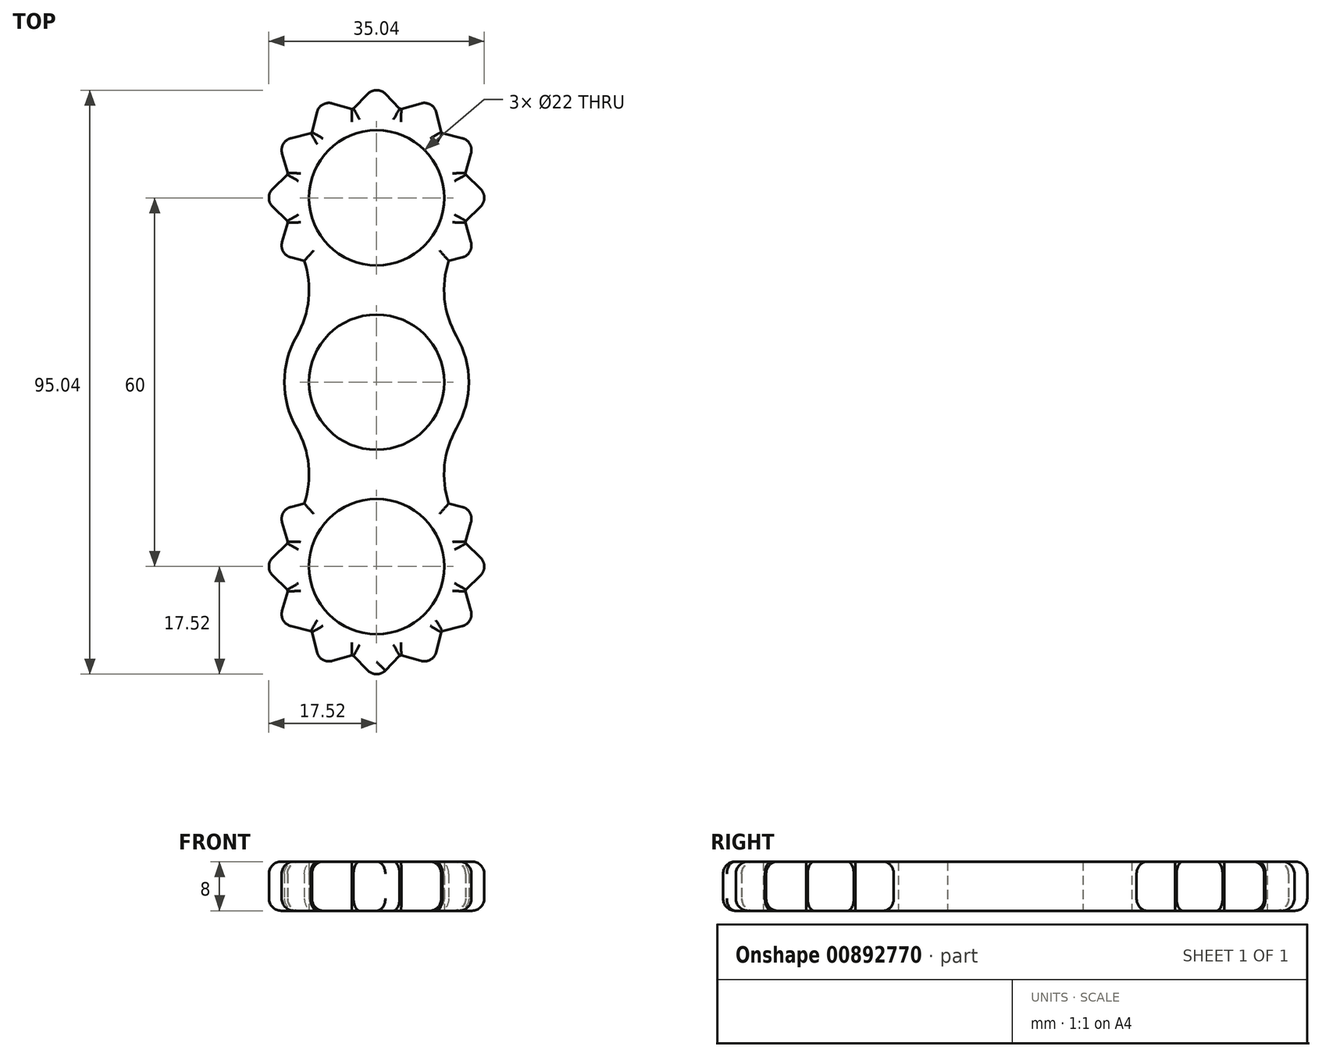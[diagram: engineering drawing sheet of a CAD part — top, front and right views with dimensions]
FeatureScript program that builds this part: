
annotation { "Feature Type Name" : "Feature", "Feature Type Description" : "" }
export const myFeature = defineFeature(function(context is Context, id is Id, definition is map)
    precondition{}
    {
        {
            var Q0;
            Q0=qCreatedBy(makeId("Top.planeOp"),FACE);
            var sketch = newSketch(context, id + "F0", { "sketchPlane" : qUnion([Q0])});
            skArc(sketch, "E0", {"start": v(-13, 7.5) * mm, "mid": v(-15, 0) * mm, "end": v(-13, -7.5) * mm});
            skArc(sketch, "E1", {"start": v(13, 22.5) * mm, "mid": v(0, 45) * mm, "end": v(-13, 22.5) * mm});
            skArc(sketch, "E2", {"start": v(-13, -22.5) * mm, "mid": v(0, -45) * mm, "end": v(13, -22.5) * mm});
            skArc(sketch, "E3", {"start": v(-13, 7.5) * mm, "mid": v(-10.98, 15) * mm, "end": v(-13, 22.5) * mm});
            skArc(sketch, "E4", {"start": v(-13, -22.5) * mm, "mid": v(-10.98, -15) * mm, "end": v(-13, -7.5) * mm});
            skArc(sketch, "E5", {"start": v(13, -7.5) * mm, "mid": v(10.98, -15) * mm, "end": v(13, -22.5) * mm});
            skArc(sketch, "E6", {"start": v(13, 22.5) * mm, "mid": v(10.98, 15) * mm, "end": v(13, 7.5) * mm});
            skArc(sketch, "E7.trimOffspring", {"start": v(13, -7.5) * mm, "mid": v(15, 0) * mm, "end": v(13, 7.5) * mm});
            skLineSegment(sketch, "E8", {"start": v(-15, 0) * mm, "end": v(15, 0) * mm, "construction": true});
            skLineSegment(sketch, "E9", {"start": v(-1.43, 46.91) * mm, "end": v(-3.76, 44.52) * mm});
            skLineSegment(sketch, "E10", {"start": v(1.43, 46.91) * mm, "end": v(3.76, 44.52) * mm});
            skPoint(sketch, "E11.visualSharp", {"position": v(0, 48.39) * mm});
            skArc(sketch, "E11.filletArc", {"start": v(1.43, 46.91) * mm, "mid": v(0, 47.52) * mm, "end": v(-1.43, 46.91) * mm});
            skArc(sketch, "E12.1.0", {"start": v(9.7, 43.93) * mm, "mid": v(8.76, 45.17) * mm, "end": v(7.21, 45.36) * mm});
            skLineSegment(sketch, "E12.1.1", {"start": v(7.21, 45.36) * mm, "end": v(4, 44.45) * mm});
            skLineSegment(sketch, "E12.1.2", {"start": v(9.7, 43.93) * mm, "end": v(10.51, 40.7) * mm});
            skArc(sketch, "E12.2.0", {"start": v(15.36, 37.21) * mm, "mid": v(15.17, 38.76) * mm, "end": v(13.93, 39.7) * mm});
            skLineSegment(sketch, "E12.2.1", {"start": v(13.93, 39.7) * mm, "end": v(10.7, 40.51) * mm});
            skLineSegment(sketch, "E12.2.2", {"start": v(15.36, 37.21) * mm, "end": v(14.45, 34) * mm});
            skArc(sketch, "E12.3.0", {"start": v(16.91, 28.57) * mm, "mid": v(17.52, 30) * mm, "end": v(16.91, 31.43) * mm});
            skLineSegment(sketch, "E12.3.1", {"start": v(16.91, 31.43) * mm, "end": v(14.52, 33.76) * mm});
            skLineSegment(sketch, "E12.3.2", {"start": v(16.91, 28.57) * mm, "end": v(14.52, 26.24) * mm});
            skArc(sketch, "E12.4.0", {"start": v(13.93, 20.3) * mm, "mid": v(15.17, 21.24) * mm, "end": v(15.36, 22.79) * mm});
            skLineSegment(sketch, "E12.4.1", {"start": v(15.36, 22.79) * mm, "end": v(14.45, 26) * mm});
            skLineSegment(sketch, "E12.4.2", {"start": v(13.93, 20.3) * mm, "end": v(11.75, 19.75) * mm});
            skArc(sketch, "E12.8.0", {"start": v(-15.36, 22.79) * mm, "mid": v(-15.17, 21.24) * mm, "end": v(-13.93, 20.3) * mm});
            skLineSegment(sketch, "E12.8.1", {"start": v(-13.93, 20.3) * mm, "end": v(-11.75, 19.75) * mm});
            skLineSegment(sketch, "E12.8.2", {"start": v(-15.36, 22.79) * mm, "end": v(-14.45, 26) * mm});
            skArc(sketch, "E12.9.0", {"start": v(-16.91, 31.43) * mm, "mid": v(-17.52, 30) * mm, "end": v(-16.91, 28.57) * mm});
            skLineSegment(sketch, "E12.9.1", {"start": v(-16.91, 28.57) * mm, "end": v(-14.52, 26.24) * mm});
            skLineSegment(sketch, "E12.9.2", {"start": v(-16.91, 31.43) * mm, "end": v(-14.52, 33.76) * mm});
            skArc(sketch, "E12.10.0", {"start": v(-13.93, 39.7) * mm, "mid": v(-15.17, 38.76) * mm, "end": v(-15.36, 37.21) * mm});
            skLineSegment(sketch, "E12.10.1", {"start": v(-15.36, 37.21) * mm, "end": v(-14.45, 34) * mm});
            skLineSegment(sketch, "E12.10.2", {"start": v(-13.93, 39.7) * mm, "end": v(-10.7, 40.51) * mm});
            skArc(sketch, "E12.11.0", {"start": v(-7.21, 45.36) * mm, "mid": v(-8.76, 45.17) * mm, "end": v(-9.7, 43.93) * mm});
            skLineSegment(sketch, "E12.11.1", {"start": v(-9.7, 43.93) * mm, "end": v(-10.51, 40.7) * mm});
            skLineSegment(sketch, "E12.11.2", {"start": v(-7.21, 45.36) * mm, "end": v(-4, 44.45) * mm});
            skLineSegment(sketch, "E12.anchor1", {"start": v(0, 30) * mm, "end": v(-1.43, 46.91) * mm, "construction": true});
            skLineSegment(sketch, "E12.anchor2", {"start": v(0, 30) * mm, "end": v(-9.7, 43.93) * mm, "construction": true});
            skPoint(sketch, "E13.orphan", {"position": v(-10.7, 19.49) * mm});
            skPoint(sketch, "E14.orphan", {"position": v(10.7, 19.49) * mm});
            skLineSegment(sketch, "E15.MirrorCS", {"start": v(-13.93, -20.3) * mm, "end": v(-11.75, -19.75) * mm});
            skArc(sketch, "E16.MirrorCS", {"start": v(-15.36, -22.79) * mm, "mid": v(-15.17, -21.24) * mm, "end": v(-13.93, -20.3) * mm});
            skLineSegment(sketch, "E17.MirrorCS", {"start": v(-15.36, -22.79) * mm, "end": v(-14.45, -26) * mm});
            skLineSegment(sketch, "E18.MirrorCS", {"start": v(-16.91, -28.57) * mm, "end": v(-14.52, -26.24) * mm});
            skArc(sketch, "E19.MirrorCS", {"start": v(-16.91, -31.43) * mm, "mid": v(-17.52, -30) * mm, "end": v(-16.91, -28.57) * mm});
            skLineSegment(sketch, "E20.MirrorCS", {"start": v(-16.91, -31.43) * mm, "end": v(-14.52, -33.76) * mm});
            skLineSegment(sketch, "E21.MirrorCS", {"start": v(-15.36, -37.21) * mm, "end": v(-14.45, -34) * mm});
            skArc(sketch, "E22.MirrorCS", {"start": v(-13.93, -39.7) * mm, "mid": v(-15.17, -38.76) * mm, "end": v(-15.36, -37.21) * mm});
            skLineSegment(sketch, "E23.MirrorCS", {"start": v(-13.93, -39.7) * mm, "end": v(-10.7, -40.51) * mm});
            skLineSegment(sketch, "E24.MirrorCS", {"start": v(-9.7, -43.93) * mm, "end": v(-10.51, -40.7) * mm});
            skArc(sketch, "E25.MirrorCS", {"start": v(-7.21, -45.36) * mm, "mid": v(-8.76, -45.17) * mm, "end": v(-9.7, -43.93) * mm});
            skLineSegment(sketch, "E26.MirrorCS", {"start": v(-7.21, -45.36) * mm, "end": v(-4, -44.45) * mm});
            skLineSegment(sketch, "E27.MirrorCS", {"start": v(-1.43, -46.91) * mm, "end": v(-3.76, -44.52) * mm});
            skArc(sketch, "E28.MirrorCS", {"start": v(1.43, -46.91) * mm, "mid": v(0, -47.52) * mm, "end": v(-1.43, -46.91) * mm});
            skLineSegment(sketch, "E29.MirrorCS", {"start": v(1.43, -46.91) * mm, "end": v(3.76, -44.52) * mm});
            skLineSegment(sketch, "E30.MirrorCS", {"start": v(7.21, -45.36) * mm, "end": v(4, -44.45) * mm});
            skArc(sketch, "E31.MirrorCS", {"start": v(9.7, -43.93) * mm, "mid": v(8.76, -45.17) * mm, "end": v(7.21, -45.36) * mm});
            skLineSegment(sketch, "E32.MirrorCS", {"start": v(9.7, -43.93) * mm, "end": v(10.51, -40.7) * mm});
            skLineSegment(sketch, "E33.MirrorCS", {"start": v(13.93, -39.7) * mm, "end": v(10.7, -40.51) * mm});
            skArc(sketch, "E34.MirrorCS", {"start": v(15.36, -37.21) * mm, "mid": v(15.17, -38.76) * mm, "end": v(13.93, -39.7) * mm});
            skLineSegment(sketch, "E35.MirrorCS", {"start": v(15.36, -37.21) * mm, "end": v(14.45, -34) * mm});
            skLineSegment(sketch, "E36.MirrorCS", {"start": v(16.91, -31.43) * mm, "end": v(14.52, -33.76) * mm});
            skArc(sketch, "E37.MirrorCS", {"start": v(16.91, -28.57) * mm, "mid": v(17.52, -30) * mm, "end": v(16.91, -31.43) * mm});
            skLineSegment(sketch, "E38.MirrorCS", {"start": v(16.91, -28.57) * mm, "end": v(14.52, -26.24) * mm});
            skLineSegment(sketch, "E39.MirrorCS", {"start": v(15.36, -22.79) * mm, "end": v(14.45, -26) * mm});
            skArc(sketch, "E40.MirrorCS", {"start": v(13.93, -20.3) * mm, "mid": v(15.17, -21.24) * mm, "end": v(15.36, -22.79) * mm});
            skLineSegment(sketch, "E41.MirrorCS", {"start": v(13.93, -20.3) * mm, "end": v(11.75, -19.75) * mm});
            skSolve(sketch);
        }
        {
            var Q0;
            {var subQ0=sQuery(id+"F0.wireOp",EDGE,"E18.MirrorCS");Q0=makeQuery(id+"F0.imprint","IMPRINT",FACE,{"disambiguationData":[TD([[makeQuery(id+"F0.imprint","IMPRINT",EDGE,{"derivedFrom":subQ0}),-1.0]])]});}
            var Q1;
            Q1=makeQuery(id+"F0.imprint","IMPRINT",FACE,{"disambiguationData":[TD([[makeQuery(id+"F0.imprint","IMPRINT",EDGE,{"derivedFrom":sQuery(id+"F0.wireOp",EDGE,"E12.10.0")}),1.0]])]});
            var Q2;
            Q2=makeQuery(id+"F0.imprint","IMPRINT",FACE,{"disambiguationData":[TD([[makeQuery(id+"F0.imprint","IMPRINT",EDGE,{"derivedFrom":sQuery(id+"F0.wireOp",EDGE,"E12.9.0")}),1.0]])]});
            var Q3;
            {var subQ23=sQuery(id+"F0.wireOp",EDGE,"E0");Q3=makeQuery(id+"F0.imprint","IMPRINT",FACE,{"disambiguationData":[TD([[makeQuery(id+"F0.imprint","IMPRINT",EDGE,{"derivedFrom":subQ23}),1.0]])]});}
            var Q4;
            {var subQ0=sQuery(id+"F0.wireOp",EDGE,"E15.MirrorCS");Q4=makeQuery(id+"F0.imprint","IMPRINT",FACE,{"disambiguationData":[TD([[makeQuery(id+"F0.imprint","IMPRINT",EDGE,{"derivedFrom":subQ0}),-1.0]])]});}
            var Q5;
            {var subQ0=sQuery(id+"F0.wireOp",EDGE,"E36.MirrorCS");Q5=makeQuery(id+"F0.imprint","IMPRINT",FACE,{"disambiguationData":[TD([[makeQuery(id+"F0.imprint","IMPRINT",EDGE,{"derivedFrom":subQ0}),-1.0]])]});}
            var Q6;
            Q6=makeQuery(id+"F0.imprint","IMPRINT",FACE,{"disambiguationData":[TD([[makeQuery(id+"F0.imprint","IMPRINT",EDGE,{"derivedFrom":sQuery(id+"F0.wireOp",EDGE,"E12.2.0")}),1.0]])]});
            var Q7;
            {var subQ0=sQuery(id+"F0.wireOp",EDGE,"E9");Q7=makeQuery(id+"F0.imprint","IMPRINT",FACE,{"disambiguationData":[TD([[makeQuery(id+"F0.imprint","IMPRINT",EDGE,{"derivedFrom":subQ0}),1.0]])]});}
            var Q8;
            Q8=makeQuery(id+"F0.imprint","IMPRINT",FACE,{"disambiguationData":[TD([[makeQuery(id+"F0.imprint","IMPRINT",EDGE,{"derivedFrom":sQuery(id+"F0.wireOp",EDGE,"E12.4.0")}),1.0]])]});
            var Q9;
            {var subQ0=sQuery(id+"F0.wireOp",EDGE,"E39.MirrorCS");Q9=makeQuery(id+"F0.imprint","IMPRINT",FACE,{"disambiguationData":[TD([[makeQuery(id+"F0.imprint","IMPRINT",EDGE,{"derivedFrom":subQ0}),-1.0]])]});}
            var Q10;
            {var subQ0=sQuery(id+"F0.wireOp",EDGE,"E30.MirrorCS");Q10=makeQuery(id+"F0.imprint","IMPRINT",FACE,{"disambiguationData":[TD([[makeQuery(id+"F0.imprint","IMPRINT",EDGE,{"derivedFrom":subQ0}),-1.0]])]});}
            var Q11;
            {var subQ0=sQuery(id+"F0.wireOp",EDGE,"E33.MirrorCS");Q11=makeQuery(id+"F0.imprint","IMPRINT",FACE,{"disambiguationData":[TD([[makeQuery(id+"F0.imprint","IMPRINT",EDGE,{"derivedFrom":subQ0}),-1.0]])]});}
            var Q12;
            {var subQ0=sQuery(id+"F0.wireOp",EDGE,"E21.MirrorCS");Q12=makeQuery(id+"F0.imprint","IMPRINT",FACE,{"disambiguationData":[TD([[makeQuery(id+"F0.imprint","IMPRINT",EDGE,{"derivedFrom":subQ0}),-1.0]])]});}
            var Q13;
            Q13=makeQuery(id+"F0.imprint","IMPRINT",FACE,{"disambiguationData":[TD([[makeQuery(id+"F0.imprint","IMPRINT",EDGE,{"derivedFrom":sQuery(id+"F0.wireOp",EDGE,"E12.3.0")}),1.0]])]});
            var Q14;
            Q14=makeQuery(id+"F0.imprint","IMPRINT",FACE,{"disambiguationData":[TD([[makeQuery(id+"F0.imprint","IMPRINT",EDGE,{"derivedFrom":sQuery(id+"F0.wireOp",EDGE,"E12.1.0")}),1.0]])]});
            var Q15;
            {var subQ0=sQuery(id+"F0.wireOp",EDGE,"E24.MirrorCS");Q15=makeQuery(id+"F0.imprint","IMPRINT",FACE,{"disambiguationData":[TD([[makeQuery(id+"F0.imprint","IMPRINT",EDGE,{"derivedFrom":subQ0}),-1.0]])]});}
            var Q16;
            Q16=makeQuery(id+"F0.imprint","IMPRINT",FACE,{"disambiguationData":[TD([[makeQuery(id+"F0.imprint","IMPRINT",EDGE,{"derivedFrom":sQuery(id+"F0.wireOp",EDGE,"E12.11.0")}),1.0]])]});
            var Q17;
            Q17=makeQuery(id+"F0.imprint","IMPRINT",FACE,{"disambiguationData":[TD([[makeQuery(id+"F0.imprint","IMPRINT",EDGE,{"derivedFrom":sQuery(id+"F0.wireOp",EDGE,"E12.8.0")}),1.0]])]});
            var Q18;
            {var subQ0=sQuery(id+"F0.wireOp",EDGE,"E27.MirrorCS");Q18=makeQuery(id+"F0.imprint","IMPRINT",FACE,{"disambiguationData":[TD([[makeQuery(id+"F0.imprint","IMPRINT",EDGE,{"derivedFrom":subQ0}),-1.0]])]});}
            extrude(context, id + "F1", {"entities" : qUnion([Q0, Q1, Q2, Q3, Q4, Q5, Q6, Q7, Q8, Q9, Q10, Q11, Q12, Q13, Q14, Q15, Q16, Q17, Q18]), "depth" : 8 * mm, "offsetDistance" : 25 * mm});
        }
        {
            var Q0;
            Q0=sQuery(id+"F0.wireOp",VERTEX,"E2.center");
            var Q1;
            Q1=sQuery(id+"F0.wireOp",VERTEX,"E0.center");
            var Q2;
            Q2=sQuery(id+"F0.wireOp",VERTEX,"E1.center");
            var Q3;
            Q3=makeQuery(id+"F1.opExtrude","SWEPT_BODY",BODY,{"disambiguationData":[OSD([sQuery(id+"F0.wireOp",EDGE,"E0"),sQuery(id+"F0.wireOp",EDGE,"E1"),sQuery(id+"F0.wireOp",EDGE,"E2"),sQuery(id+"F0.wireOp",EDGE,"E3"),sQuery(id+"F0.wireOp",EDGE,"E4"),sQuery(id+"F0.wireOp",EDGE,"E5"),sQuery(id+"F0.wireOp",EDGE,"E6"),sQuery(id+"F0.wireOp",EDGE,"E7.trimOffspring"),sQuery(id+"F0.wireOp",EDGE,"E9"),sQuery(id+"F0.wireOp",EDGE,"E10"),sQuery(id+"F0.wireOp",EDGE,"E11.filletArc"),sQuery(id+"F0.wireOp",EDGE,"E12.1.0"),sQuery(id+"F0.wireOp",EDGE,"E12.1.1"),sQuery(id+"F0.wireOp",EDGE,"E12.1.2"),sQuery(id+"F0.wireOp",EDGE,"E12.2.0"),sQuery(id+"F0.wireOp",EDGE,"E12.2.1"),sQuery(id+"F0.wireOp",EDGE,"E12.2.2"),sQuery(id+"F0.wireOp",EDGE,"E12.3.0"),sQuery(id+"F0.wireOp",EDGE,"E12.3.1"),sQuery(id+"F0.wireOp",EDGE,"E12.3.2"),sQuery(id+"F0.wireOp",EDGE,"E12.4.0"),sQuery(id+"F0.wireOp",EDGE,"E12.4.1"),sQuery(id+"F0.wireOp",EDGE,"E12.4.2"),sQuery(id+"F0.wireOp",EDGE,"E12.8.0"),sQuery(id+"F0.wireOp",EDGE,"E12.8.1"),sQuery(id+"F0.wireOp",EDGE,"E12.8.2"),sQuery(id+"F0.wireOp",EDGE,"E12.9.0"),sQuery(id+"F0.wireOp",EDGE,"E12.9.1"),sQuery(id+"F0.wireOp",EDGE,"E12.9.2"),sQuery(id+"F0.wireOp",EDGE,"E12.10.0"),sQuery(id+"F0.wireOp",EDGE,"E12.10.1"),sQuery(id+"F0.wireOp",EDGE,"E12.10.2"),sQuery(id+"F0.wireOp",EDGE,"E12.11.0"),sQuery(id+"F0.wireOp",EDGE,"E12.11.1"),sQuery(id+"F0.wireOp",EDGE,"E12.11.2"),sQuery(id+"F0.wireOp",EDGE,"E15.MirrorCS"),sQuery(id+"F0.wireOp",EDGE,"E16.MirrorCS"),sQuery(id+"F0.wireOp",EDGE,"E17.MirrorCS"),sQuery(id+"F0.wireOp",EDGE,"E18.MirrorCS"),sQuery(id+"F0.wireOp",EDGE,"E19.MirrorCS"),sQuery(id+"F0.wireOp",EDGE,"E20.MirrorCS"),sQuery(id+"F0.wireOp",EDGE,"E21.MirrorCS"),sQuery(id+"F0.wireOp",EDGE,"E22.MirrorCS"),sQuery(id+"F0.wireOp",EDGE,"E23.MirrorCS"),sQuery(id+"F0.wireOp",EDGE,"E24.MirrorCS"),sQuery(id+"F0.wireOp",EDGE,"E25.MirrorCS"),sQuery(id+"F0.wireOp",EDGE,"E26.MirrorCS"),sQuery(id+"F0.wireOp",EDGE,"E27.MirrorCS"),sQuery(id+"F0.wireOp",EDGE,"E28.MirrorCS"),sQuery(id+"F0.wireOp",EDGE,"E29.MirrorCS"),sQuery(id+"F0.wireOp",EDGE,"E30.MirrorCS"),sQuery(id+"F0.wireOp",EDGE,"E31.MirrorCS"),sQuery(id+"F0.wireOp",EDGE,"E32.MirrorCS"),sQuery(id+"F0.wireOp",EDGE,"E33.MirrorCS"),sQuery(id+"F0.wireOp",EDGE,"E34.MirrorCS"),sQuery(id+"F0.wireOp",EDGE,"E35.MirrorCS"),sQuery(id+"F0.wireOp",EDGE,"E36.MirrorCS"),sQuery(id+"F0.wireOp",EDGE,"E37.MirrorCS"),sQuery(id+"F0.wireOp",EDGE,"E38.MirrorCS"),sQuery(id+"F0.wireOp",EDGE,"E39.MirrorCS"),sQuery(id+"F0.wireOp",EDGE,"E40.MirrorCS"),sQuery(id+"F0.wireOp",EDGE,"E41.MirrorCS")])]});
            hole(context, id + "F2", {"style" : HoleStyle.SIMPLE, "endStyle" : HoleEndStyle.THROUGH, "oppositeDirection" : true, "holeDiameter" : 22 * mm, "majorDiameter" : 5 * mm, "isTappedThrough" : true, "tappedDepth" : 12 * mm, "tapClearance" : 3, "locations" : qUnion([Q0, Q1, Q2]), "scope" : qUnion([Q3])});
        }
        {
            var Q0;
            Q0=makeQuery(id+"F1.opExtrude","CAP_EDGE",EDGE,{"disambiguationData":[OSD([sQuery(id+"F0.wireOp",EDGE,"E7.trimOffspring")])],"isStart":false});
            var Q1;
            Q1=makeQuery(id+"F1.opExtrude","CAP_EDGE",EDGE,{"disambiguationData":[OSD([sQuery(id+"F0.wireOp",EDGE,"E5")])],"isStart":false});
            var Q2;
            Q2=makeQuery(id+"F1.opExtrude","CAP_EDGE",EDGE,{"disambiguationData":[OSD([sQuery(id+"F0.wireOp",EDGE,"E41.MirrorCS")])],"isStart":false});
            var Q3;
            Q3=makeQuery(id+"F1.opExtrude","CAP_EDGE",EDGE,{"disambiguationData":[OSD([sQuery(id+"F0.wireOp",EDGE,"E39.MirrorCS")])],"isStart":false});
            var Q4;
            {var subQ0=sQuery(id+"F0.wireOp",EDGE,"E2");Q4=makeQuery(id+"F1.opExtrude","CAP_EDGE",EDGE,{"disambiguationData":[OSD([subQ0]),TDD([makeQuery(id+"F0.imprint","IMPRINT",EDGE,{"disambiguationData":[TD([[makeQuery(id+"F0.imprint","INTERSECT",VERTEX,{"derivedFrom":[subQ0,sQuery(id+"F0.wireOp",EDGE,"E38.MirrorCS")]}),-1.0]])],"derivedFrom":subQ0})])],"isStart":false});}
            var Q5;
            Q5=makeQuery(id+"F1.opExtrude","CAP_EDGE",EDGE,{"disambiguationData":[OSD([sQuery(id+"F0.wireOp",EDGE,"E38.MirrorCS")])],"isStart":false});
            var Q6;
            Q6=makeQuery(id+"F1.opExtrude","CAP_EDGE",EDGE,{"disambiguationData":[OSD([sQuery(id+"F0.wireOp",EDGE,"E36.MirrorCS")])],"isStart":false});
            var Q7;
            {var subQ0=sQuery(id+"F0.wireOp",EDGE,"E2");Q7=makeQuery(id+"F1.opExtrude","CAP_EDGE",EDGE,{"disambiguationData":[OSD([subQ0]),TDD([makeQuery(id+"F0.imprint","IMPRINT",EDGE,{"disambiguationData":[TD([[makeQuery(id+"F0.imprint","INTERSECT",VERTEX,{"derivedFrom":[subQ0,sQuery(id+"F0.wireOp",EDGE,"E35.MirrorCS")]}),-1.0]])],"derivedFrom":subQ0})])],"isStart":false});}
            var Q8;
            Q8=makeQuery(id+"F1.opExtrude","CAP_EDGE",EDGE,{"disambiguationData":[OSD([sQuery(id+"F0.wireOp",EDGE,"E35.MirrorCS")])],"isStart":false});
            var Q9;
            Q9=makeQuery(id+"F1.opExtrude","CAP_EDGE",EDGE,{"disambiguationData":[OSD([sQuery(id+"F0.wireOp",EDGE,"E33.MirrorCS")])],"isStart":false});
            var Q10;
            {var subQ0=sQuery(id+"F0.wireOp",EDGE,"E2");Q10=makeQuery(id+"F1.opExtrude","CAP_EDGE",EDGE,{"disambiguationData":[OSD([subQ0]),TDD([makeQuery(id+"F0.imprint","IMPRINT",EDGE,{"disambiguationData":[TD([[makeQuery(id+"F0.imprint","INTERSECT",VERTEX,{"derivedFrom":[subQ0,sQuery(id+"F0.wireOp",EDGE,"E32.MirrorCS")]}),-1.0]])],"derivedFrom":subQ0})])],"isStart":false});}
            var Q11;
            Q11=makeQuery(id+"F1.opExtrude","CAP_EDGE",EDGE,{"disambiguationData":[OSD([sQuery(id+"F0.wireOp",EDGE,"E32.MirrorCS")])],"isStart":false});
            var Q12;
            Q12=makeQuery(id+"F1.opExtrude","CAP_EDGE",EDGE,{"disambiguationData":[OSD([sQuery(id+"F0.wireOp",EDGE,"E30.MirrorCS")])],"isStart":false});
            var Q13;
            {var subQ0=sQuery(id+"F0.wireOp",EDGE,"E2");Q13=makeQuery(id+"F1.opExtrude","CAP_EDGE",EDGE,{"disambiguationData":[OSD([subQ0]),TDD([makeQuery(id+"F0.imprint","IMPRINT",EDGE,{"disambiguationData":[TD([[makeQuery(id+"F0.imprint","INTERSECT",VERTEX,{"derivedFrom":[subQ0,sQuery(id+"F0.wireOp",EDGE,"E29.MirrorCS")]}),-1.0]])],"derivedFrom":subQ0})])],"isStart":false});}
            var Q14;
            Q14=makeQuery(id+"F1.opExtrude","CAP_EDGE",EDGE,{"disambiguationData":[OSD([sQuery(id+"F0.wireOp",EDGE,"E29.MirrorCS")])],"isStart":false});
            var Q15;
            Q15=makeQuery(id+"F1.opExtrude","CAP_EDGE",EDGE,{"disambiguationData":[OSD([sQuery(id+"F0.wireOp",EDGE,"E27.MirrorCS")])],"isStart":false});
            var Q16;
            {var subQ0=sQuery(id+"F0.wireOp",EDGE,"E2");Q16=makeQuery(id+"F1.opExtrude","CAP_EDGE",EDGE,{"disambiguationData":[OSD([subQ0]),TDD([makeQuery(id+"F0.imprint","IMPRINT",EDGE,{"disambiguationData":[TD([[makeQuery(id+"F0.imprint","INTERSECT",VERTEX,{"derivedFrom":[subQ0,sQuery(id+"F0.wireOp",EDGE,"E26.MirrorCS")]}),-1.0]])],"derivedFrom":subQ0})])],"isStart":false});}
            var Q17;
            Q17=makeQuery(id+"F1.opExtrude","CAP_EDGE",EDGE,{"disambiguationData":[OSD([sQuery(id+"F0.wireOp",EDGE,"E26.MirrorCS")])],"isStart":false});
            var Q18;
            {var subQ0=sQuery(id+"F0.wireOp",EDGE,"E2");Q18=makeQuery(id+"F1.opExtrude","CAP_EDGE",EDGE,{"disambiguationData":[OSD([subQ0]),TDD([makeQuery(id+"F0.imprint","IMPRINT",EDGE,{"disambiguationData":[TD([[makeQuery(id+"F0.imprint","INTERSECT",VERTEX,{"derivedFrom":[subQ0,sQuery(id+"F0.wireOp",EDGE,"E23.MirrorCS")]}),-1.0]])],"derivedFrom":subQ0})])],"isStart":false});}
            var Q19;
            Q19=makeQuery(id+"F1.opExtrude","CAP_EDGE",EDGE,{"disambiguationData":[OSD([sQuery(id+"F0.wireOp",EDGE,"E24.MirrorCS")])],"isStart":false});
            var Q20;
            Q20=makeQuery(id+"F1.opExtrude","CAP_EDGE",EDGE,{"disambiguationData":[OSD([sQuery(id+"F0.wireOp",EDGE,"E23.MirrorCS")])],"isStart":false});
            var Q21;
            Q21=makeQuery(id+"F1.opExtrude","CAP_EDGE",EDGE,{"disambiguationData":[OSD([sQuery(id+"F0.wireOp",EDGE,"E21.MirrorCS")])],"isStart":false});
            var Q22;
            {var subQ0=sQuery(id+"F0.wireOp",EDGE,"E2");Q22=makeQuery(id+"F1.opExtrude","CAP_EDGE",EDGE,{"disambiguationData":[OSD([subQ0]),TDD([makeQuery(id+"F0.imprint","IMPRINT",EDGE,{"disambiguationData":[TD([[makeQuery(id+"F0.imprint","INTERSECT",VERTEX,{"derivedFrom":[subQ0,sQuery(id+"F0.wireOp",EDGE,"E20.MirrorCS")]}),-1.0]])],"derivedFrom":subQ0})])],"isStart":false});}
            var Q23;
            Q23=makeQuery(id+"F1.opExtrude","CAP_EDGE",EDGE,{"disambiguationData":[OSD([sQuery(id+"F0.wireOp",EDGE,"E20.MirrorCS")])],"isStart":false});
            var Q24;
            {var subQ0=sQuery(id+"F0.wireOp",EDGE,"E2");Q24=makeQuery(id+"F1.opExtrude","CAP_EDGE",EDGE,{"disambiguationData":[OSD([subQ0]),TDD([makeQuery(id+"F0.imprint","IMPRINT",EDGE,{"disambiguationData":[TD([[makeQuery(id+"F0.imprint","INTERSECT",VERTEX,{"derivedFrom":[subQ0,sQuery(id+"F0.wireOp",EDGE,"E17.MirrorCS")]}),-1.0]])],"derivedFrom":subQ0})])],"isStart":false});}
            var Q25;
            Q25=makeQuery(id+"F1.opExtrude","CAP_EDGE",EDGE,{"disambiguationData":[OSD([sQuery(id+"F0.wireOp",EDGE,"E17.MirrorCS")])],"isStart":false});
            var Q26;
            Q26=makeQuery(id+"F1.opExtrude","CAP_EDGE",EDGE,{"disambiguationData":[OSD([sQuery(id+"F0.wireOp",EDGE,"E15.MirrorCS")])],"isStart":false});
            var Q27;
            Q27=makeQuery(id+"F1.opExtrude","CAP_EDGE",EDGE,{"disambiguationData":[OSD([sQuery(id+"F0.wireOp",EDGE,"E4")])],"isStart":false});
            var Q28;
            Q28=makeQuery(id+"F1.opExtrude","CAP_EDGE",EDGE,{"disambiguationData":[OSD([sQuery(id+"F0.wireOp",EDGE,"E0")])],"isStart":false});
            var Q29;
            Q29=makeQuery(id+"F1.opExtrude","CAP_EDGE",EDGE,{"disambiguationData":[OSD([sQuery(id+"F0.wireOp",EDGE,"E3")])],"isStart":false});
            var Q30;
            Q30=makeQuery(id+"F1.opExtrude","CAP_EDGE",EDGE,{"disambiguationData":[OSD([sQuery(id+"F0.wireOp",EDGE,"E12.8.1")])],"isStart":false});
            var Q31;
            Q31=makeQuery(id+"F1.opExtrude","CAP_EDGE",EDGE,{"disambiguationData":[OSD([sQuery(id+"F0.wireOp",EDGE,"E12.8.2")])],"isStart":false});
            var Q32;
            Q32=makeQuery(id+"F1.opExtrude","CAP_EDGE",EDGE,{"disambiguationData":[OSD([sQuery(id+"F0.wireOp",EDGE,"E12.9.1")])],"isStart":false});
            var Q33;
            Q33=makeQuery(id+"F1.opExtrude","CAP_EDGE",EDGE,{"disambiguationData":[OSD([sQuery(id+"F0.wireOp",EDGE,"E12.9.2")])],"isStart":false});
            var Q34;
            Q34=makeQuery(id+"F1.opExtrude","CAP_EDGE",EDGE,{"disambiguationData":[OSD([sQuery(id+"F0.wireOp",EDGE,"E12.10.2")])],"isStart":false});
            var Q35;
            Q35=makeQuery(id+"F1.opExtrude","CAP_EDGE",EDGE,{"disambiguationData":[OSD([sQuery(id+"F0.wireOp",EDGE,"E12.10.1")])],"isStart":false});
            var Q36;
            {var subQ0=sQuery(id+"F0.wireOp",EDGE,"E1");Q36=makeQuery(id+"F1.opExtrude","CAP_EDGE",EDGE,{"disambiguationData":[OSD([subQ0]),TDD([makeQuery(id+"F0.imprint","IMPRINT",EDGE,{"disambiguationData":[TD([[makeQuery(id+"F0.imprint","INTERSECT",VERTEX,{"derivedFrom":[subQ0,sQuery(id+"F0.wireOp",EDGE,"E12.8.2")]}),1.0]])],"derivedFrom":subQ0})])],"isStart":false});}
            var Q37;
            {var subQ0=sQuery(id+"F0.wireOp",EDGE,"E1");Q37=makeQuery(id+"F1.opExtrude","CAP_EDGE",EDGE,{"disambiguationData":[OSD([subQ0]),TDD([makeQuery(id+"F0.imprint","IMPRINT",EDGE,{"disambiguationData":[TD([[makeQuery(id+"F0.imprint","INTERSECT",VERTEX,{"derivedFrom":[subQ0,sQuery(id+"F0.wireOp",EDGE,"E12.9.2")]}),1.0]])],"derivedFrom":subQ0})])],"isStart":false});}
            var Q38;
            Q38=makeQuery(id+"F1.opExtrude","CAP_EDGE",EDGE,{"disambiguationData":[OSD([sQuery(id+"F0.wireOp",EDGE,"E12.11.1")])],"isStart":false});
            var Q39;
            {var subQ0=sQuery(id+"F0.wireOp",EDGE,"E1");Q39=makeQuery(id+"F1.opExtrude","CAP_EDGE",EDGE,{"disambiguationData":[OSD([subQ0]),TDD([makeQuery(id+"F0.imprint","IMPRINT",EDGE,{"disambiguationData":[TD([[makeQuery(id+"F0.imprint","INTERSECT",VERTEX,{"derivedFrom":[subQ0,sQuery(id+"F0.wireOp",EDGE,"E12.10.2")]}),1.0]])],"derivedFrom":subQ0})])],"isStart":false});}
            var Q40;
            Q40=makeQuery(id+"F1.opExtrude","CAP_EDGE",EDGE,{"disambiguationData":[OSD([sQuery(id+"F0.wireOp",EDGE,"E12.11.2")])],"isStart":false});
            var Q41;
            {var subQ0=sQuery(id+"F0.wireOp",EDGE,"E1");Q41=makeQuery(id+"F1.opExtrude","CAP_EDGE",EDGE,{"disambiguationData":[OSD([subQ0]),TDD([makeQuery(id+"F0.imprint","IMPRINT",EDGE,{"disambiguationData":[TD([[makeQuery(id+"F0.imprint","INTERSECT",VERTEX,{"derivedFrom":[subQ0,sQuery(id+"F0.wireOp",EDGE,"E9")]}),-1.0]])],"derivedFrom":subQ0})])],"isStart":false});}
            var Q42;
            Q42=makeQuery(id+"F1.opExtrude","CAP_EDGE",EDGE,{"disambiguationData":[OSD([sQuery(id+"F0.wireOp",EDGE,"E9")])],"isStart":false});
            var Q43;
            Q43=makeQuery(id+"F1.opExtrude","CAP_EDGE",EDGE,{"disambiguationData":[OSD([sQuery(id+"F0.wireOp",EDGE,"E10")])],"isStart":false});
            var Q44;
            {var subQ0=sQuery(id+"F0.wireOp",EDGE,"E1");Q44=makeQuery(id+"F1.opExtrude","CAP_EDGE",EDGE,{"disambiguationData":[OSD([subQ0]),TDD([makeQuery(id+"F0.imprint","IMPRINT",EDGE,{"disambiguationData":[TD([[makeQuery(id+"F0.imprint","INTERSECT",VERTEX,{"derivedFrom":[subQ0,sQuery(id+"F0.wireOp",EDGE,"E10")]}),1.0]])],"derivedFrom":subQ0})])],"isStart":false});}
            var Q45;
            Q45=makeQuery(id+"F1.opExtrude","CAP_EDGE",EDGE,{"disambiguationData":[OSD([sQuery(id+"F0.wireOp",EDGE,"E12.1.1")])],"isStart":false});
            var Q46;
            Q46=makeQuery(id+"F1.opExtrude","CAP_EDGE",EDGE,{"disambiguationData":[OSD([sQuery(id+"F0.wireOp",EDGE,"E12.1.2")])],"isStart":false});
            var Q47;
            Q47=makeQuery(id+"F1.opExtrude","CAP_EDGE",EDGE,{"disambiguationData":[OSD([sQuery(id+"F0.wireOp",EDGE,"E12.2.1")])],"isStart":false});
            var Q48;
            {var subQ0=sQuery(id+"F0.wireOp",EDGE,"E1");Q48=makeQuery(id+"F1.opExtrude","CAP_EDGE",EDGE,{"disambiguationData":[OSD([subQ0]),TDD([makeQuery(id+"F0.imprint","IMPRINT",EDGE,{"disambiguationData":[TD([[makeQuery(id+"F0.imprint","INTERSECT",VERTEX,{"derivedFrom":[subQ0,sQuery(id+"F0.wireOp",EDGE,"E12.1.2")]}),1.0]])],"derivedFrom":subQ0})])],"isStart":false});}
            var Q49;
            Q49=makeQuery(id+"F1.opExtrude","CAP_EDGE",EDGE,{"disambiguationData":[OSD([sQuery(id+"F0.wireOp",EDGE,"E12.2.2")])],"isStart":false});
            var Q50;
            {var subQ0=sQuery(id+"F0.wireOp",EDGE,"E1");Q50=makeQuery(id+"F1.opExtrude","CAP_EDGE",EDGE,{"disambiguationData":[OSD([subQ0]),TDD([makeQuery(id+"F0.imprint","IMPRINT",EDGE,{"disambiguationData":[TD([[makeQuery(id+"F0.imprint","INTERSECT",VERTEX,{"derivedFrom":[subQ0,sQuery(id+"F0.wireOp",EDGE,"E12.2.2")]}),1.0]])],"derivedFrom":subQ0})])],"isStart":false});}
            var Q51;
            Q51=makeQuery(id+"F1.opExtrude","CAP_EDGE",EDGE,{"disambiguationData":[OSD([sQuery(id+"F0.wireOp",EDGE,"E12.3.1")])],"isStart":false});
            var Q52;
            Q52=makeQuery(id+"F1.opExtrude","CAP_EDGE",EDGE,{"disambiguationData":[OSD([sQuery(id+"F0.wireOp",EDGE,"E12.3.2")])],"isStart":false});
            var Q53;
            {var subQ0=sQuery(id+"F0.wireOp",EDGE,"E1");Q53=makeQuery(id+"F1.opExtrude","CAP_EDGE",EDGE,{"disambiguationData":[OSD([subQ0]),TDD([makeQuery(id+"F0.imprint","IMPRINT",EDGE,{"disambiguationData":[TD([[makeQuery(id+"F0.imprint","INTERSECT",VERTEX,{"derivedFrom":[subQ0,sQuery(id+"F0.wireOp",EDGE,"E12.3.2")]}),1.0]])],"derivedFrom":subQ0})])],"isStart":false});}
            var Q54;
            Q54=makeQuery(id+"F1.opExtrude","CAP_EDGE",EDGE,{"disambiguationData":[OSD([sQuery(id+"F0.wireOp",EDGE,"E12.4.1")])],"isStart":false});
            var Q55;
            Q55=makeQuery(id+"F1.opExtrude","CAP_EDGE",EDGE,{"disambiguationData":[OSD([sQuery(id+"F0.wireOp",EDGE,"E12.4.2")])],"isStart":false});
            var Q56;
            Q56=makeQuery(id+"F1.opExtrude","CAP_EDGE",EDGE,{"disambiguationData":[OSD([sQuery(id+"F0.wireOp",EDGE,"E6")])],"isStart":false});
            var Q57;
            Q57=makeQuery(id+"F1.opExtrude","CAP_EDGE",EDGE,{"disambiguationData":[OSD([sQuery(id+"F0.wireOp",EDGE,"E0")])],"isStart":true});
            var Q58;
            Q58=makeQuery(id+"F1.opExtrude","CAP_EDGE",EDGE,{"disambiguationData":[OSD([sQuery(id+"F0.wireOp",EDGE,"E3")])],"isStart":true});
            var Q59;
            Q59=makeQuery(id+"F1.opExtrude","CAP_EDGE",EDGE,{"disambiguationData":[OSD([sQuery(id+"F0.wireOp",EDGE,"E12.8.1")])],"isStart":true});
            var Q60;
            Q60=makeQuery(id+"F1.opExtrude","CAP_EDGE",EDGE,{"disambiguationData":[OSD([sQuery(id+"F0.wireOp",EDGE,"E12.8.2")])],"isStart":true});
            var Q61;
            Q61=makeQuery(id+"F1.opExtrude","CAP_EDGE",EDGE,{"disambiguationData":[OSD([sQuery(id+"F0.wireOp",EDGE,"E12.9.1")])],"isStart":true});
            var Q62;
            {var subQ0=sQuery(id+"F0.wireOp",EDGE,"E1");Q62=makeQuery(id+"F1.opExtrude","CAP_EDGE",EDGE,{"disambiguationData":[OSD([subQ0]),TDD([makeQuery(id+"F0.imprint","IMPRINT",EDGE,{"disambiguationData":[TD([[makeQuery(id+"F0.imprint","INTERSECT",VERTEX,{"derivedFrom":[subQ0,sQuery(id+"F0.wireOp",EDGE,"E12.8.2")]}),1.0]])],"derivedFrom":subQ0})])],"isStart":true});}
            var Q63;
            Q63=makeQuery(id+"F1.opExtrude","CAP_EDGE",EDGE,{"disambiguationData":[OSD([sQuery(id+"F0.wireOp",EDGE,"E12.9.2")])],"isStart":true});
            var Q64;
            {var subQ0=sQuery(id+"F0.wireOp",EDGE,"E1");Q64=makeQuery(id+"F1.opExtrude","CAP_EDGE",EDGE,{"disambiguationData":[OSD([subQ0]),TDD([makeQuery(id+"F0.imprint","IMPRINT",EDGE,{"disambiguationData":[TD([[makeQuery(id+"F0.imprint","INTERSECT",VERTEX,{"derivedFrom":[subQ0,sQuery(id+"F0.wireOp",EDGE,"E12.9.2")]}),1.0]])],"derivedFrom":subQ0})])],"isStart":true});}
            var Q65;
            Q65=makeQuery(id+"F1.opExtrude","CAP_EDGE",EDGE,{"disambiguationData":[OSD([sQuery(id+"F0.wireOp",EDGE,"E12.10.1")])],"isStart":true});
            var Q66;
            Q66=makeQuery(id+"F1.opExtrude","CAP_EDGE",EDGE,{"disambiguationData":[OSD([sQuery(id+"F0.wireOp",EDGE,"E12.10.2")])],"isStart":true});
            var Q67;
            {var subQ0=sQuery(id+"F0.wireOp",EDGE,"E1");Q67=makeQuery(id+"F1.opExtrude","CAP_EDGE",EDGE,{"disambiguationData":[OSD([subQ0]),TDD([makeQuery(id+"F0.imprint","IMPRINT",EDGE,{"disambiguationData":[TD([[makeQuery(id+"F0.imprint","INTERSECT",VERTEX,{"derivedFrom":[subQ0,sQuery(id+"F0.wireOp",EDGE,"E12.10.2")]}),1.0]])],"derivedFrom":subQ0})])],"isStart":true});}
            var Q68;
            Q68=makeQuery(id+"F1.opExtrude","CAP_EDGE",EDGE,{"disambiguationData":[OSD([sQuery(id+"F0.wireOp",EDGE,"E12.11.1")])],"isStart":true});
            var Q69;
            Q69=makeQuery(id+"F1.opExtrude","CAP_EDGE",EDGE,{"disambiguationData":[OSD([sQuery(id+"F0.wireOp",EDGE,"E12.11.2")])],"isStart":true});
            var Q70;
            {var subQ0=sQuery(id+"F0.wireOp",EDGE,"E1");Q70=makeQuery(id+"F1.opExtrude","CAP_EDGE",EDGE,{"disambiguationData":[OSD([subQ0]),TDD([makeQuery(id+"F0.imprint","IMPRINT",EDGE,{"disambiguationData":[TD([[makeQuery(id+"F0.imprint","INTERSECT",VERTEX,{"derivedFrom":[subQ0,sQuery(id+"F0.wireOp",EDGE,"E9")]}),-1.0]])],"derivedFrom":subQ0})])],"isStart":true});}
            var Q71;
            Q71=makeQuery(id+"F1.opExtrude","CAP_EDGE",EDGE,{"disambiguationData":[OSD([sQuery(id+"F0.wireOp",EDGE,"E9")])],"isStart":true});
            var Q72;
            Q72=makeQuery(id+"F1.opExtrude","CAP_EDGE",EDGE,{"disambiguationData":[OSD([sQuery(id+"F0.wireOp",EDGE,"E10")])],"isStart":true});
            var Q73;
            {var subQ0=sQuery(id+"F0.wireOp",EDGE,"E1");Q73=makeQuery(id+"F1.opExtrude","CAP_EDGE",EDGE,{"disambiguationData":[OSD([subQ0]),TDD([makeQuery(id+"F0.imprint","IMPRINT",EDGE,{"disambiguationData":[TD([[makeQuery(id+"F0.imprint","INTERSECT",VERTEX,{"derivedFrom":[subQ0,sQuery(id+"F0.wireOp",EDGE,"E10")]}),1.0]])],"derivedFrom":subQ0})])],"isStart":true});}
            var Q74;
            Q74=makeQuery(id+"F1.opExtrude","CAP_EDGE",EDGE,{"disambiguationData":[OSD([sQuery(id+"F0.wireOp",EDGE,"E12.1.1")])],"isStart":true});
            var Q75;
            Q75=makeQuery(id+"F1.opExtrude","CAP_EDGE",EDGE,{"disambiguationData":[OSD([sQuery(id+"F0.wireOp",EDGE,"E12.1.2")])],"isStart":true});
            var Q76;
            {var subQ0=sQuery(id+"F0.wireOp",EDGE,"E1");Q76=makeQuery(id+"F1.opExtrude","CAP_EDGE",EDGE,{"disambiguationData":[OSD([subQ0]),TDD([makeQuery(id+"F0.imprint","IMPRINT",EDGE,{"disambiguationData":[TD([[makeQuery(id+"F0.imprint","INTERSECT",VERTEX,{"derivedFrom":[subQ0,sQuery(id+"F0.wireOp",EDGE,"E12.1.2")]}),1.0]])],"derivedFrom":subQ0})])],"isStart":true});}
            var Q77;
            Q77=makeQuery(id+"F1.opExtrude","CAP_EDGE",EDGE,{"disambiguationData":[OSD([sQuery(id+"F0.wireOp",EDGE,"E12.2.1")])],"isStart":true});
            var Q78;
            Q78=makeQuery(id+"F1.opExtrude","CAP_EDGE",EDGE,{"disambiguationData":[OSD([sQuery(id+"F0.wireOp",EDGE,"E12.3.2")])],"isStart":true});
            var Q79;
            {var subQ0=sQuery(id+"F0.wireOp",EDGE,"E1");Q79=makeQuery(id+"F1.opExtrude","CAP_EDGE",EDGE,{"disambiguationData":[OSD([subQ0]),TDD([makeQuery(id+"F0.imprint","IMPRINT",EDGE,{"disambiguationData":[TD([[makeQuery(id+"F0.imprint","INTERSECT",VERTEX,{"derivedFrom":[subQ0,sQuery(id+"F0.wireOp",EDGE,"E12.3.2")]}),1.0]])],"derivedFrom":subQ0})])],"isStart":true});}
            var Q80;
            Q80=makeQuery(id+"F1.opExtrude","CAP_EDGE",EDGE,{"disambiguationData":[OSD([sQuery(id+"F0.wireOp",EDGE,"E12.4.1")])],"isStart":true});
            var Q81;
            Q81=makeQuery(id+"F1.opExtrude","CAP_EDGE",EDGE,{"disambiguationData":[OSD([sQuery(id+"F0.wireOp",EDGE,"E12.4.2")])],"isStart":true});
            var Q82;
            Q82=makeQuery(id+"F1.opExtrude","CAP_EDGE",EDGE,{"disambiguationData":[OSD([sQuery(id+"F0.wireOp",EDGE,"E6")])],"isStart":true});
            var Q83;
            Q83=makeQuery(id+"F1.opExtrude","CAP_EDGE",EDGE,{"disambiguationData":[OSD([sQuery(id+"F0.wireOp",EDGE,"E5")])],"isStart":true});
            var Q84;
            Q84=makeQuery(id+"F1.opExtrude","CAP_EDGE",EDGE,{"disambiguationData":[OSD([sQuery(id+"F0.wireOp",EDGE,"E4")])],"isStart":true});
            var Q85;
            Q85=makeQuery(id+"F1.opExtrude","CAP_EDGE",EDGE,{"disambiguationData":[OSD([sQuery(id+"F0.wireOp",EDGE,"E7.trimOffspring")])],"isStart":true});
            var Q86;
            Q86=makeQuery(id+"F1.opExtrude","CAP_EDGE",EDGE,{"disambiguationData":[OSD([sQuery(id+"F0.wireOp",EDGE,"E41.MirrorCS")])],"isStart":true});
            var Q87;
            Q87=makeQuery(id+"F1.opExtrude","CAP_EDGE",EDGE,{"disambiguationData":[OSD([sQuery(id+"F0.wireOp",EDGE,"E39.MirrorCS")])],"isStart":true});
            var Q88;
            {var subQ0=sQuery(id+"F0.wireOp",EDGE,"E2");Q88=makeQuery(id+"F1.opExtrude","CAP_EDGE",EDGE,{"disambiguationData":[OSD([subQ0]),TDD([makeQuery(id+"F0.imprint","IMPRINT",EDGE,{"disambiguationData":[TD([[makeQuery(id+"F0.imprint","INTERSECT",VERTEX,{"derivedFrom":[subQ0,sQuery(id+"F0.wireOp",EDGE,"E38.MirrorCS")]}),-1.0]])],"derivedFrom":subQ0})])],"isStart":true});}
            var Q89;
            Q89=makeQuery(id+"F1.opExtrude","CAP_EDGE",EDGE,{"disambiguationData":[OSD([sQuery(id+"F0.wireOp",EDGE,"E38.MirrorCS")])],"isStart":true});
            var Q90;
            Q90=makeQuery(id+"F1.opExtrude","CAP_EDGE",EDGE,{"disambiguationData":[OSD([sQuery(id+"F0.wireOp",EDGE,"E36.MirrorCS")])],"isStart":true});
            var Q91;
            {var subQ0=sQuery(id+"F0.wireOp",EDGE,"E2");Q91=makeQuery(id+"F1.opExtrude","CAP_EDGE",EDGE,{"disambiguationData":[OSD([subQ0]),TDD([makeQuery(id+"F0.imprint","IMPRINT",EDGE,{"disambiguationData":[TD([[makeQuery(id+"F0.imprint","INTERSECT",VERTEX,{"derivedFrom":[subQ0,sQuery(id+"F0.wireOp",EDGE,"E35.MirrorCS")]}),-1.0]])],"derivedFrom":subQ0})])],"isStart":true});}
            var Q92;
            Q92=makeQuery(id+"F1.opExtrude","CAP_EDGE",EDGE,{"disambiguationData":[OSD([sQuery(id+"F0.wireOp",EDGE,"E33.MirrorCS")])],"isStart":true});
            var Q93;
            Q93=makeQuery(id+"F1.opExtrude","CAP_EDGE",EDGE,{"disambiguationData":[OSD([sQuery(id+"F0.wireOp",EDGE,"E32.MirrorCS")])],"isStart":true});
            var Q94;
            {var subQ0=sQuery(id+"F0.wireOp",EDGE,"E2");Q94=makeQuery(id+"F1.opExtrude","CAP_EDGE",EDGE,{"disambiguationData":[OSD([subQ0]),TDD([makeQuery(id+"F0.imprint","IMPRINT",EDGE,{"disambiguationData":[TD([[makeQuery(id+"F0.imprint","INTERSECT",VERTEX,{"derivedFrom":[subQ0,sQuery(id+"F0.wireOp",EDGE,"E32.MirrorCS")]}),-1.0]])],"derivedFrom":subQ0})])],"isStart":true});}
            var Q95;
            Q95=makeQuery(id+"F1.opExtrude","CAP_EDGE",EDGE,{"disambiguationData":[OSD([sQuery(id+"F0.wireOp",EDGE,"E27.MirrorCS")])],"isStart":true});
            var Q96;
            Q96=makeQuery(id+"F1.opExtrude","CAP_EDGE",EDGE,{"disambiguationData":[OSD([sQuery(id+"F0.wireOp",EDGE,"E26.MirrorCS")])],"isStart":true});
            var Q97;
            Q97=makeQuery(id+"F1.opExtrude","CAP_EDGE",EDGE,{"disambiguationData":[OSD([sQuery(id+"F0.wireOp",EDGE,"E24.MirrorCS")])],"isStart":true});
            var Q98;
            Q98=makeQuery(id+"F1.opExtrude","CAP_EDGE",EDGE,{"disambiguationData":[OSD([sQuery(id+"F0.wireOp",EDGE,"E23.MirrorCS")])],"isStart":true});
            var Q99;
            Q99=makeQuery(id+"F1.opExtrude","CAP_EDGE",EDGE,{"disambiguationData":[OSD([sQuery(id+"F0.wireOp",EDGE,"E17.MirrorCS")])],"isStart":true});
            var Q100;
            Q100=makeQuery(id+"F1.opExtrude","CAP_EDGE",EDGE,{"disambiguationData":[OSD([sQuery(id+"F0.wireOp",EDGE,"E18.MirrorCS")])],"isStart":true});
            var Q101;
            Q101=makeQuery(id+"F1.opExtrude","CAP_EDGE",EDGE,{"disambiguationData":[OSD([sQuery(id+"F0.wireOp",EDGE,"E15.MirrorCS")])],"isStart":true});
            var Q102;
            {var subQ0=sQuery(id+"F0.wireOp",EDGE,"E2");Q102=makeQuery(id+"F1.opExtrude","CAP_EDGE",EDGE,{"disambiguationData":[OSD([subQ0]),TDD([makeQuery(id+"F0.imprint","IMPRINT",EDGE,{"disambiguationData":[TD([[makeQuery(id+"F0.imprint","INTERSECT",VERTEX,{"derivedFrom":[subQ0,sQuery(id+"F0.wireOp",EDGE,"E29.MirrorCS")]}),-1.0]])],"derivedFrom":subQ0})])],"isStart":true});}
            var Q103;
            {var subQ0=sQuery(id+"F0.wireOp",EDGE,"E2");Q103=makeQuery(id+"F1.opExtrude","CAP_EDGE",EDGE,{"disambiguationData":[OSD([subQ0]),TDD([makeQuery(id+"F0.imprint","IMPRINT",EDGE,{"disambiguationData":[TD([[makeQuery(id+"F0.imprint","INTERSECT",VERTEX,{"derivedFrom":[subQ0,sQuery(id+"F0.wireOp",EDGE,"E26.MirrorCS")]}),-1.0]])],"derivedFrom":subQ0})])],"isStart":true});}
            var Q104;
            {var subQ0=sQuery(id+"F0.wireOp",EDGE,"E2");Q104=makeQuery(id+"F1.opExtrude","CAP_EDGE",EDGE,{"disambiguationData":[OSD([subQ0]),TDD([makeQuery(id+"F0.imprint","IMPRINT",EDGE,{"disambiguationData":[TD([[makeQuery(id+"F0.imprint","INTERSECT",VERTEX,{"derivedFrom":[subQ0,sQuery(id+"F0.wireOp",EDGE,"E23.MirrorCS")]}),-1.0]])],"derivedFrom":subQ0})])],"isStart":true});}
            var Q105;
            {var subQ0=sQuery(id+"F0.wireOp",EDGE,"E2");Q105=makeQuery(id+"F1.opExtrude","CAP_EDGE",EDGE,{"disambiguationData":[OSD([subQ0]),TDD([makeQuery(id+"F0.imprint","IMPRINT",EDGE,{"disambiguationData":[TD([[makeQuery(id+"F0.imprint","INTERSECT",VERTEX,{"derivedFrom":[subQ0,sQuery(id+"F0.wireOp",EDGE,"E20.MirrorCS")]}),-1.0]])],"derivedFrom":subQ0})])],"isStart":true});}
            var Q106;
            {var subQ0=sQuery(id+"F0.wireOp",EDGE,"E2");Q106=makeQuery(id+"F1.opExtrude","CAP_EDGE",EDGE,{"disambiguationData":[OSD([subQ0]),TDD([makeQuery(id+"F0.imprint","IMPRINT",EDGE,{"disambiguationData":[TD([[makeQuery(id+"F0.imprint","INTERSECT",VERTEX,{"derivedFrom":[subQ0,sQuery(id+"F0.wireOp",EDGE,"E17.MirrorCS")]}),-1.0]])],"derivedFrom":subQ0})])],"isStart":true});}
            var Q107;
            Q107=makeQuery(id+"F1.opExtrude","CAP_EDGE",EDGE,{"disambiguationData":[OSD([sQuery(id+"F0.wireOp",EDGE,"E18.MirrorCS")])],"isStart":false});
            var Q108;
            Q108=makeQuery(id+"F1.opExtrude","CAP_EDGE",EDGE,{"disambiguationData":[OSD([sQuery(id+"F0.wireOp",EDGE,"E20.MirrorCS")])],"isStart":true});
            var Q109;
            Q109=makeQuery(id+"F1.opExtrude","CAP_EDGE",EDGE,{"disambiguationData":[OSD([sQuery(id+"F0.wireOp",EDGE,"E21.MirrorCS")])],"isStart":true});
            var Q110;
            {var subQ0=sQuery(id+"F0.wireOp",EDGE,"E1");Q110=makeQuery(id+"F1.opExtrude","CAP_EDGE",EDGE,{"disambiguationData":[OSD([subQ0]),TDD([makeQuery(id+"F0.imprint","IMPRINT",EDGE,{"disambiguationData":[TD([[makeQuery(id+"F0.imprint","INTERSECT",VERTEX,{"derivedFrom":[subQ0,sQuery(id+"F0.wireOp",EDGE,"E12.2.2")]}),1.0]])],"derivedFrom":subQ0})])],"isStart":true});}
            fillet(context, id + "F3", {"entities" : qUnion([Q0, Q1, Q2, Q3, Q4, Q5, Q6, Q7, Q8, Q9, Q10, Q11, Q12, Q13, Q14, Q15, Q16, Q17, Q18, Q19, Q20, Q21, Q22, Q23, Q24, Q25, Q26, Q27, Q28, Q29, Q30, Q31, Q32, Q33, Q34, Q35, Q36, Q37, Q38, Q39, Q40, Q41, Q42, Q43, Q44, Q45, Q46, Q47, Q48, Q49, Q50, Q51, Q52, Q53, Q54, Q55, Q56, Q57, Q58, Q59, Q60, Q61, Q62, Q63, Q64, Q65, Q66, Q67, Q68, Q69, Q70, Q71, Q72, Q73, Q74, Q75, Q76, Q77, Q78, Q79, Q80, Q81, Q82, Q83, Q84, Q85, Q86, Q87, Q88, Q89, Q90, Q91, Q92, Q93, Q94, Q95, Q96, Q97, Q98, Q99, Q100, Q101, Q102, Q103, Q104, Q105, Q106, Q107, Q108, Q109, Q110]), "radius" : 2 * mm, "tangentPropagation" : true, "allowEdgeOverflow" : false});
        }
    });
